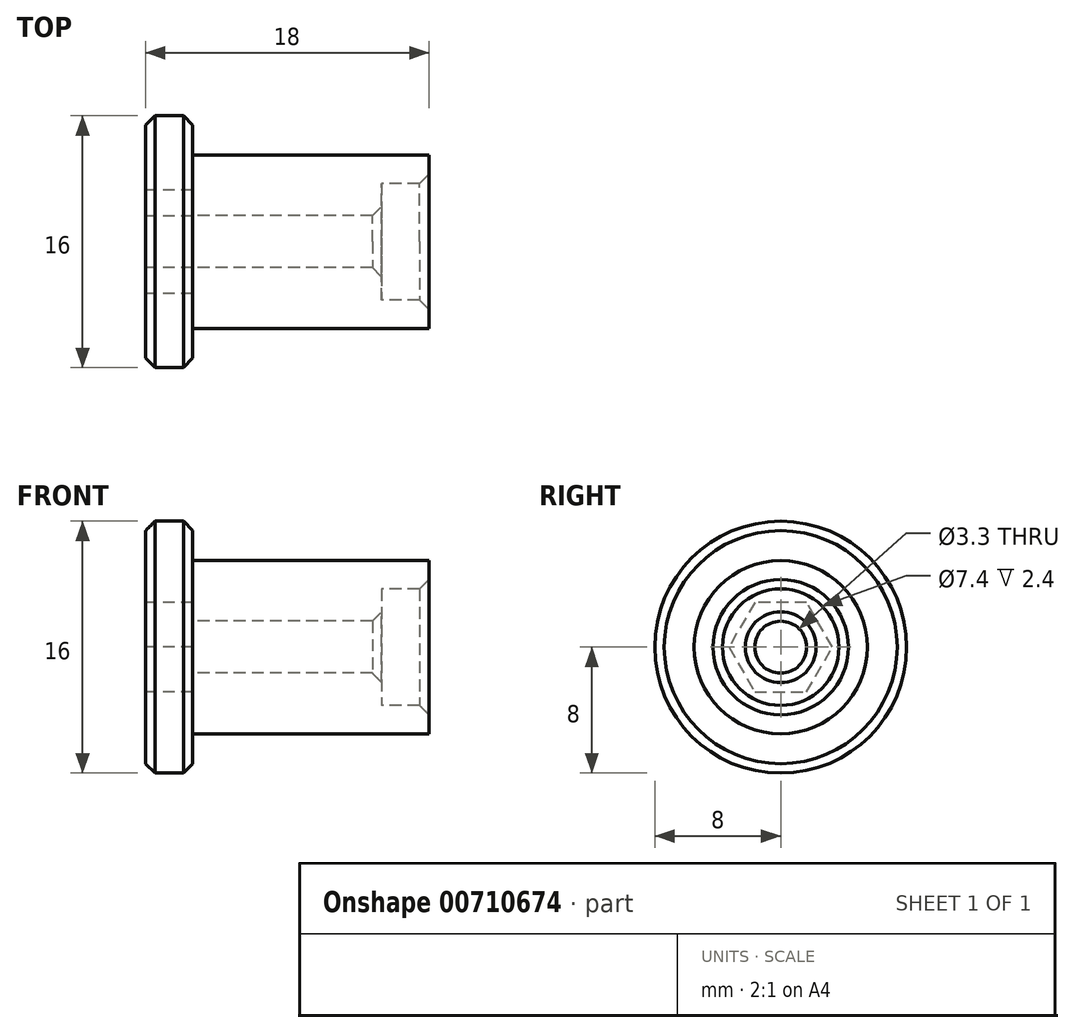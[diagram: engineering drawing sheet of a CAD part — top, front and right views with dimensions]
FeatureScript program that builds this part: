
annotation { "Feature Type Name" : "Feature", "Feature Type Description" : "" }
export const myFeature = defineFeature(function(context is Context, id is Id, definition is map)
    precondition{}
    {
        {
            var Q0;
            Q0=qCreatedBy(makeId("Front.planeOp"),FACE);
            var sketch = newSketch(context, id + "F0", { "sketchPlane" : qUnion([Q0])});
            skLineSegment(sketch, "E0", {"start": v(0, 8) * mm, "end": v(3, 8) * mm});
            skLineSegment(sketch, "E1", {"start": v(3, 8) * mm, "end": v(3, 5.5) * mm});
            skLineSegment(sketch, "E2", {"start": v(3, 5.5) * mm, "end": v(18, 5.5) * mm});
            skLineSegment(sketch, "E3", {"start": v(15, 1.65) * mm, "end": v(0, 1.65) * mm});
            skLineSegment(sketch, "E4", {"start": v(0, 1.65) * mm, "end": v(0, 8) * mm});
            skLineSegment(sketch, "E5", {"start": v(0, 0) * mm, "end": v(13.74, 0) * mm, "construction": true});
            skLineSegment(sketch, "E6", {"start": v(18, 5.5) * mm, "end": v(18, 3.7) * mm});
            skLineSegment(sketch, "E7", {"start": v(18, 3.7) * mm, "end": v(15, 3.7) * mm});
            skLineSegment(sketch, "E8", {"start": v(15, 3.7) * mm, "end": v(15, 1.65) * mm});
            skSolve(sketch);
        }
        {
            var Q0;
            Q0 = qSketchRegion(id + "F0", true);
            var Q1;
            Q1=sQuery(id+"F0.wireOp",EDGE,"E5");
            revolve(context, id + "F1", {"surfaceOperationType" : NewSurfaceOperationType.NEW, "entities" : qUnion([Q0]), "axis" : qUnion([Q1]), "revolveType" : RevolveType.FULL});
        }
        {
            var Q0;
            Q0=makeQuery(id+"F1.opRevolve","SWEPT_FACE",FACE,{"disambiguationData":[OSD([sQuery(id+"F0.wireOp",EDGE,"E4")])]});
            var sketch = newSketch(context, id + "F2", { "sketchPlane" : qUnion([Q0])});
            skCircle(sketch, "E9.cCircle", {"center": v(0, 0) * mm, "radius": 2.85 * mm, "construction": true});
            skLineSegment(sketch, "E9.0", {"start": v(1.65, -2.85) * mm, "end": v(-1.65, -2.85) * mm});
            skLineSegment(sketch, "E9.1", {"start": v(-1.65, -2.85) * mm, "end": v(-3.3, 0) * mm});
            skLineSegment(sketch, "E9.2", {"start": v(-3.3, 0) * mm, "end": v(-1.65, 2.85) * mm});
            skLineSegment(sketch, "E9.3", {"start": v(-1.65, 2.85) * mm, "end": v(1.65, 2.85) * mm});
            skLineSegment(sketch, "E9.4", {"start": v(1.65, 2.85) * mm, "end": v(3.3, 0) * mm});
            skLineSegment(sketch, "E9.5", {"start": v(3.3, 0) * mm, "end": v(1.65, -2.85) * mm});
            skPoint(sketch, "E9.0.midPoint", {"position": v(0, -2.85) * mm});
            skSolve(sketch);
        }
        {
            var Q0;
            Q0 = qSketchRegion(id + "F2", true);
            extrude(context, id + "F3", {"entities" : qUnion([Q0]), "operationType" : NewBodyOperationType.REMOVE, "oppositeDirection" : true, "depth" : 3 * mm, "offsetDistance" : 25 * mm});
        }
        {
            var Q0;
            Q0=makeQuery(id+"F1.opRevolve","SWEPT_EDGE",EDGE,{"disambiguationData":[OSD([sQuery(id+"F0.wireOp",EDGE,"E0"),sQuery(id+"F0.wireOp",EDGE,"E4")])]});
            var Q1;
            Q1=makeQuery(id+"F1.opRevolve","SWEPT_EDGE",EDGE,{"disambiguationData":[OSD([sQuery(id+"F0.wireOp",EDGE,"E6"),sQuery(id+"F0.wireOp",EDGE,"E7")])]});
            var Q2;
            Q2=makeQuery(id+"F1.opRevolve","SWEPT_EDGE",EDGE,{"disambiguationData":[OSD([sQuery(id+"F0.wireOp",EDGE,"E3"),sQuery(id+"F0.wireOp",EDGE,"E8")])]});
            var Q3;
            Q3=makeQuery(id+"F1.opRevolve","SWEPT_EDGE",EDGE,{"disambiguationData":[OSD([sQuery(id+"F0.wireOp",EDGE,"E0"),sQuery(id+"F0.wireOp",EDGE,"E1")])]});
            chamfer(context, id + "F4", {"entities" : qUnion([Q0, Q1, Q2, Q3]), "width" : 0.6 * mm, "tangentPropagation" : true});
        }
    });
